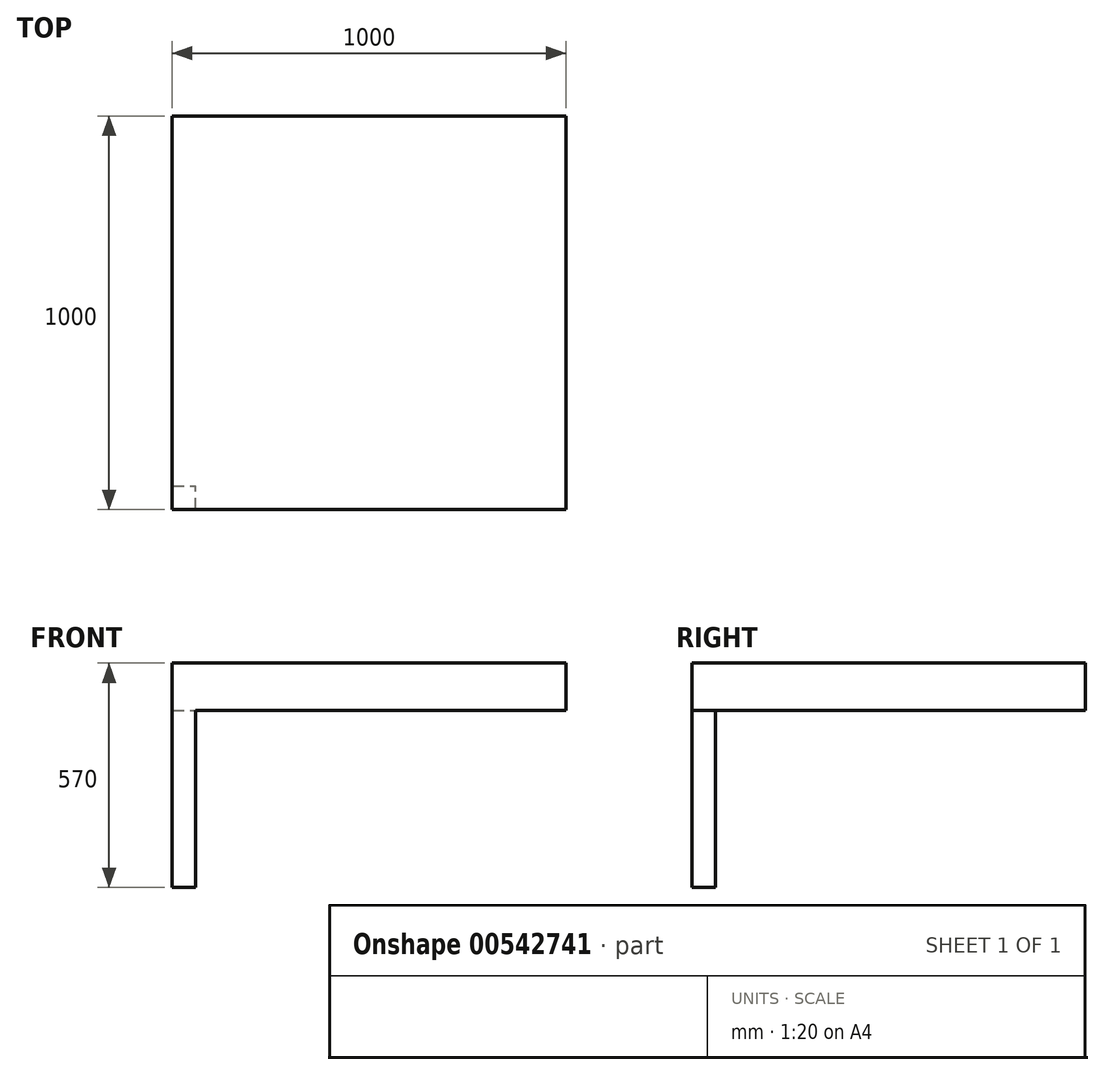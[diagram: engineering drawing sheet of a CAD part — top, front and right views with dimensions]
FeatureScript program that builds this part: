
annotation { "Feature Type Name" : "Feature", "Feature Type Description" : "" }
export const myFeature = defineFeature(function(context is Context, id is Id, definition is map)
    precondition{}
    {
        {
            var Q0;
            Q0=qCreatedBy(makeId("Top.planeOp"),FACE);
            var sketch = newSketch(context, id + "F0", { "sketchPlane" : qUnion([Q0])});
            skLineSegment(sketch, "E0.bottom", {"start": v(500, 500) * mm, "end": v(-500, 500) * mm});
            skLineSegment(sketch, "E0.top", {"start": v(500, -500) * mm, "end": v(-500, -500) * mm});
            skLineSegment(sketch, "E0.left", {"start": v(500, 500) * mm, "end": v(500, -500) * mm});
            skLineSegment(sketch, "E0.right", {"start": v(-500, 500) * mm, "end": v(-500, -500) * mm});
            skPoint(sketch, "E0.middle", {"position": v(0, 0) * mm});
            skSolve(sketch);
        }
        {
            var Q0;
            Q0 = qSketchRegion(id + "F0", true);
            extrude(context, id + "F1", {"entities" : qUnion([Q0]), "depth" : 120 * mm, "offsetDistance" : 25 * mm});
        }
        {
            var Q0;
            Q0=makeQuery(id+"F1.opExtrude","CAP_FACE",FACE,{"disambiguationData":[OSD([sQuery(id+"F0.wireOp",EDGE,"E0.bottom"),sQuery(id+"F0.wireOp",EDGE,"E0.top"),sQuery(id+"F0.wireOp",EDGE,"E0.left"),sQuery(id+"F0.wireOp",EDGE,"E0.right")])],"isStart":true});
            var sketch = newSketch(context, id + "F2", { "sketchPlane" : qUnion([Q0])});
            skLineSegment(sketch, "E1.bottom", {"start": v(-500, 500) * mm, "end": v(-440, 500) * mm});
            skLineSegment(sketch, "E1.top", {"start": v(-500, 440) * mm, "end": v(-440, 440) * mm});
            skLineSegment(sketch, "E1.left", {"start": v(-500, 500) * mm, "end": v(-500, 440) * mm});
            skLineSegment(sketch, "E1.right", {"start": v(-440, 500) * mm, "end": v(-440, 440) * mm});
            skSolve(sketch);
        }
        {
            var Q0;
            Q0 = qSketchRegion(id + "F2", true);
            extrude(context, id + "F3", {"entities" : qUnion([Q0]), "operationType" : NewBodyOperationType.ADD, "depth" : 450 * mm, "offsetDistance" : 25 * mm});
        }
        {
            var Q0;
            Q0=qCreatedBy(makeId("Front.planeOp"),FACE);
            var sketch = newSketch(context, id + "F4", { "sketchPlane" : qUnion([Q0])});
            skLineSegment(sketch, "E2", {"start": v(0, 0) * mm, "end": v(0, -90.1) * mm});
            skSolve(sketch);
        }
    });
